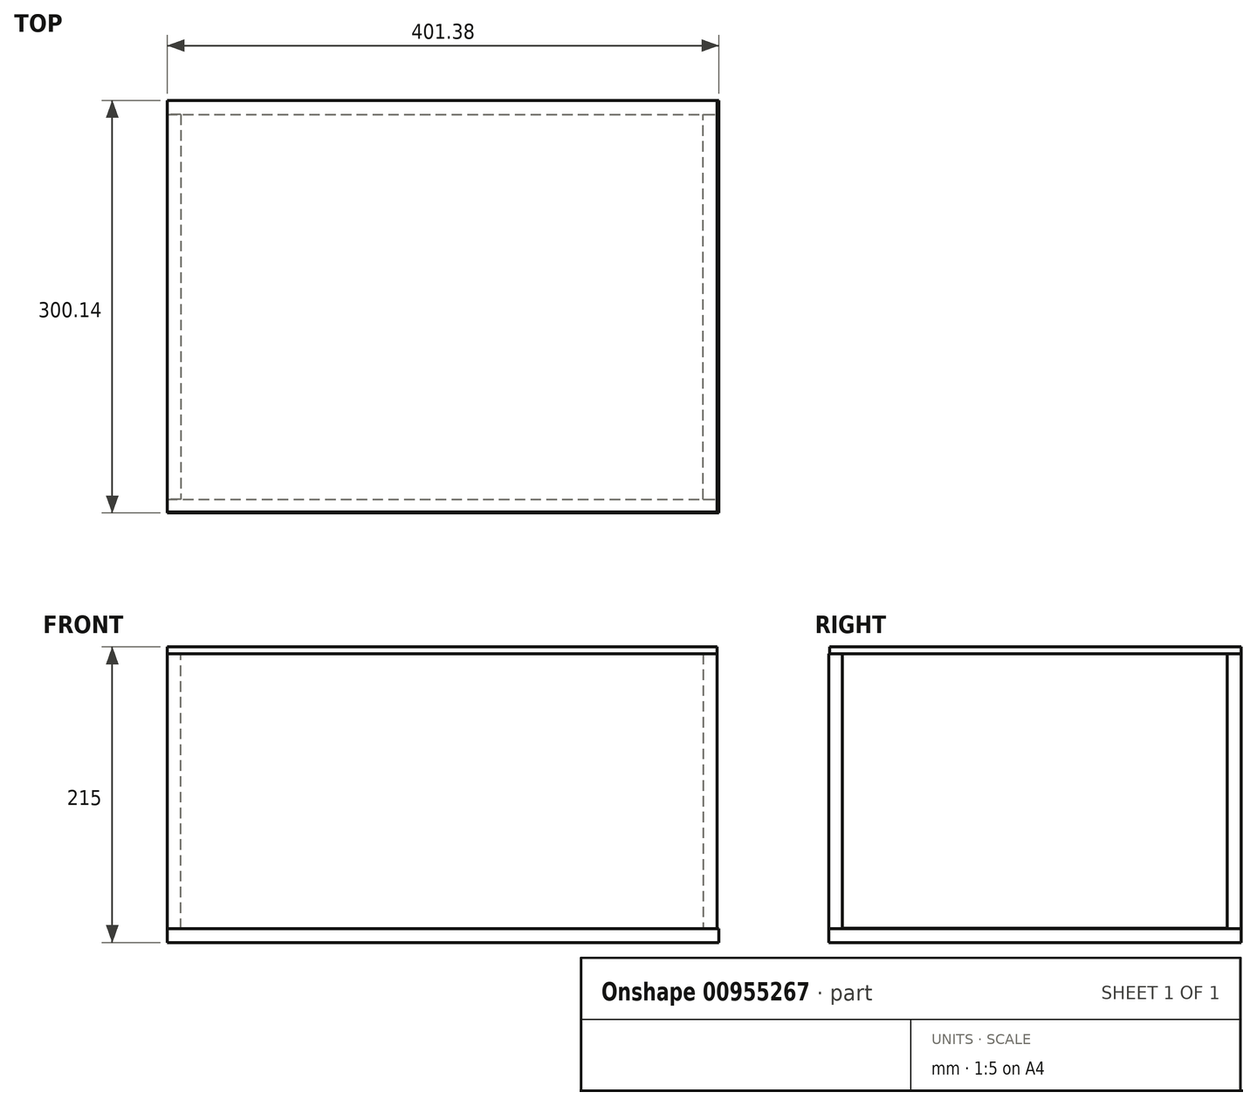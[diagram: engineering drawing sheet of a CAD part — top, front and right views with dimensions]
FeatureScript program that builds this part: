
annotation { "Feature Type Name" : "Feature", "Feature Type Description" : "" }
export const myFeature = defineFeature(function(context is Context, id is Id, definition is map)
    precondition{}
    {
        {
            var Q0;
            Q0=qCreatedBy(makeId("Right.planeOp"),FACE);
            var sketch = newSketch(context, id + "F0", { "sketchPlane" : qUnion([Q0])});
            skLineSegment(sketch, "E0.bottom", {"start": v(140, -100) * mm, "end": v(-140, -100) * mm});
            skLineSegment(sketch, "E0.top", {"start": v(140, 100) * mm, "end": v(-140, 100) * mm});
            skLineSegment(sketch, "E0.left", {"start": v(140, -100) * mm, "end": v(140, 100) * mm});
            skLineSegment(sketch, "E0.right", {"start": v(-140, -100) * mm, "end": v(-140, 100) * mm});
            skPoint(sketch, "E0.middle", {"position": v(0, 0) * mm});
            skSolve(sketch);
        }
        {
            var Q0;
            Q0=makeQuery(id+"F0.imprint","IMPRINT",FACE,{"disambiguationData":[TD([[makeQuery(id+"F0.imprint","IMPRINT",EDGE,{"derivedFrom":sQuery(id+"F0.wireOp",EDGE,"E0.bottom")}),-1.0]])]});
            extrude(context, id + "F1", {"entities" : qUnion([Q0]), "depth" : 10 * mm, "offsetDistance" : 25 * mm});
        }
        {
            var Q0;
            Q0=makeQuery(id+"F1.opExtrude","SWEPT_FACE",FACE,{"disambiguationData":[OSD([sQuery(id+"F0.wireOp",EDGE,"E0.right")])]});
            var sketch = newSketch(context, id + "F2", { "sketchPlane" : qUnion([Q0])});
            skLineSegment(sketch, "E1.bottom", {"start": v(0, 100) * mm, "end": v(400, 100) * mm});
            skLineSegment(sketch, "E1.top", {"start": v(0, -100) * mm, "end": v(400, -100) * mm});
            skLineSegment(sketch, "E1.left", {"start": v(0, 100) * mm, "end": v(0, -100) * mm});
            skLineSegment(sketch, "E1.right", {"start": v(400, 100) * mm, "end": v(400, -100) * mm});
            skSolve(sketch);
        }
        {
            var Q0;
            {var subQ2=sQuery(id+"F2.wireOp",EDGE,"E1.right");Q0=makeQuery(id+"F2.imprint","IMPRINT",FACE,{"disambiguationData":[TD([[makeQuery(id+"F2.imprint","IMPRINT",EDGE,{"derivedFrom":subQ2}),-1.0]])]});}
            var Q1;
            {var subQ0=sQuery(id+"F2.wireOp",EDGE,"E1.left");Q1=makeQuery(id+"F2.imprint","IMPRINT",FACE,{"disambiguationData":[TD([[makeQuery(id+"F2.imprint","IMPRINT",EDGE,{"derivedFrom":subQ0}),-1.0]])]});}
            extrude(context, id + "F3", {"entities" : qUnion([Q0, Q1]), "depth" : 10 * mm, "offsetDistance" : 25 * mm});
        }
        {
            var Q0;
            Q0=makeQuery(id+"F3.opExtrude","SWEPT_BODY",BODY,{"disambiguationData":[OSD([sQuery(id+"F0.wireOp",EDGE,"E0.right"),sQuery(id+"F2.wireOp",EDGE,"E1.bottom"),sQuery(id+"F2.wireOp",EDGE,"E1.top"),sQuery(id+"F2.wireOp",EDGE,"E1.right")])]});
            var Q1;
            Q1=qCreatedBy(makeId("Front.planeOp"),FACE);
            mirror(context, id + "F4", {"entities" : qUnion([Q0]), "mirrorPlane" : qUnion([Q1])});
        }
        {
            var Q0;
            Q0=makeQuery(id+"F3.opExtrude","SWEPT_FACE",FACE,{"disambiguationData":[OSD([sQuery(id+"F2.wireOp",EDGE,"E1.right")])]});
            var sketch = newSketch(context, id + "F5", { "sketchPlane" : qUnion([Q0])});
            skLineSegment(sketch, "E2.bottom", {"start": v(-140, 100) * mm, "end": v(140.05, 100) * mm});
            skLineSegment(sketch, "E2.top", {"start": v(-140, -99.59) * mm, "end": v(140.05, -99.59) * mm});
            skLineSegment(sketch, "E2.left", {"start": v(-140, 100) * mm, "end": v(-140, -99.59) * mm});
            skLineSegment(sketch, "E2.right", {"start": v(140.05, 100) * mm, "end": v(140.05, -99.59) * mm});
            skSolve(sketch);
        }
        {
            var Q0;
            Q0=makeQuery(id+"F5.imprint","IMPRINT",FACE,{"disambiguationData":[TD([[makeQuery(id+"F5.imprint","IMPRINT",EDGE,{"derivedFrom":sQuery(id+"F5.wireOp",EDGE,"E2.bottom")}),-1.0]])]});
            extrude(context, id + "F6", {"entities" : qUnion([Q0]), "oppositeDirection" : true, "depth" : 10 * mm, "offsetDistance" : 25 * mm});
        }
        {
            var Q0;
            Q0=makeQuery(id+"F3.opExtrude","SWEPT_FACE",FACE,{"disambiguationData":[OSD([sQuery(id+"F2.wireOp",EDGE,"E1.top")])]});
            var sketch = newSketch(context, id + "F7", { "sketchPlane" : qUnion([Q0])});
            skLineSegment(sketch, "E3.bottom", {"start": v(0, 150) * mm, "end": v(401.38, 150) * mm});
            skLineSegment(sketch, "E3.top", {"start": v(0, -150.14) * mm, "end": v(401.38, -150.14) * mm});
            skLineSegment(sketch, "E3.left", {"start": v(0, 150) * mm, "end": v(0, -150.14) * mm});
            skLineSegment(sketch, "E3.right", {"start": v(401.38, 150) * mm, "end": v(401.38, -150.14) * mm});
            skSolve(sketch);
        }
        {
            var Q0;
            {var subQ4=sQuery(id+"F7.wireOp",EDGE,"E3.top");Q0=makeQuery(id+"F7.imprint","IMPRINT",FACE,{"disambiguationData":[TD([[makeQuery(id+"F7.imprint","IMPRINT",EDGE,{"derivedFrom":subQ4}),1.0]])]});}
            var Q1;
            {var subQ3=sQuery(id+"F2.wireOp",EDGE,"E1.top");var subQ5=makeQuery(id+"F3.opExtrude","CAP_EDGE",EDGE,{"disambiguationData":[OSD([subQ3])],"isStart":true});Q1=makeQuery(id+"F7.imprint","IMPRINT",FACE,{"disambiguationData":[TD([[makeQuery(id+"F7.imprint","IMPRINT",EDGE,{"derivedFrom":subQ5}),1.0]])]});}
            extrude(context, id + "F8", {"entities" : qUnion([Q0, Q1]), "depth" : 10 * mm, "offsetDistance" : 25 * mm});
        }
        {
            var Q0;
            Q0=makeQuery(id+"F4.opPattern","COPY",FACE,{"derivedFrom":makeQuery(id+"F3.opExtrude","SWEPT_FACE",FACE,{"disambiguationData":[OSD([sQuery(id+"F2.wireOp",EDGE,"E1.bottom")])]}),"instanceName":"1"});
            var sketch = newSketch(context, id + "F9", { "sketchPlane" : qUnion([Q0])});
            skLineSegment(sketch, "E4.bottom", {"start": v(400, 150) * mm, "end": v(0, 150) * mm});
            skLineSegment(sketch, "E4.top", {"start": v(400, -149.18) * mm, "end": v(0, -149.18) * mm});
            skLineSegment(sketch, "E4.left", {"start": v(400, 150) * mm, "end": v(400, -149.18) * mm});
            skLineSegment(sketch, "E4.right", {"start": v(0, 150) * mm, "end": v(0, -149.18) * mm});
            skSolve(sketch);
        }
        {
            var Q0;
            {var subQ0=sQuery(id+"F9.wireOp",EDGE,"E4.top");Q0=makeQuery(id+"F9.imprint","IMPRINT",FACE,{"disambiguationData":[TD([[makeQuery(id+"F9.imprint","IMPRINT",EDGE,{"derivedFrom":subQ0}),-1.0]])]});}
            var Q1;
            {var subQ0=sQuery(id+"F9.wireOp",EDGE,"E4.bottom");Q1=makeQuery(id+"F9.imprint","IMPRINT",FACE,{"disambiguationData":[TD([[makeQuery(id+"F9.imprint","IMPRINT",EDGE,{"derivedFrom":subQ0}),-1.0]])]});}
            extrude(context, id + "F10", {"entities" : qUnion([Q0, Q1]), "depth" : 5 * mm, "offsetDistance" : 25 * mm});
        }
    });
